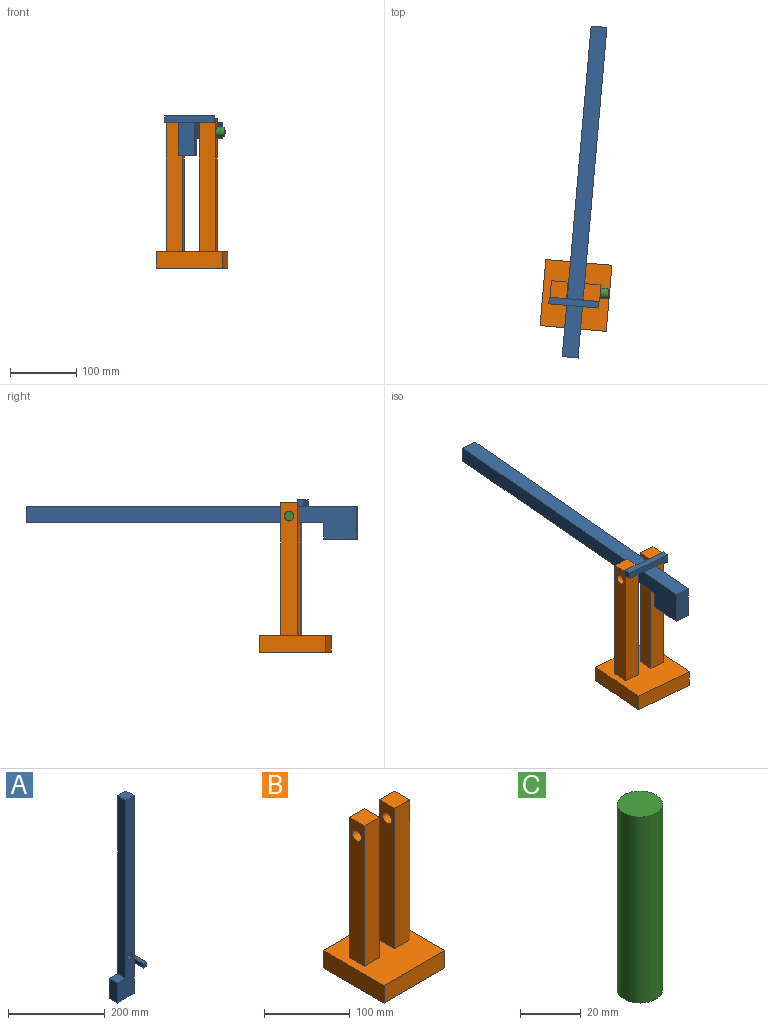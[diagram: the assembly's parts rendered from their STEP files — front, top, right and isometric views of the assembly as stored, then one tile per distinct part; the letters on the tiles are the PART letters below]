
ASSEMBLY  parts=3 mates=6
PART A: 17 faces, bbox 59x75x500 mm
  f0: plane 77.5x24mm, normal (1,0,0), area 1860mm2, adj f3,f4,f6,f11
  f1: plane 412.5x24mm, normal (1,0,0), area 9900mm2, adj f3,f4,f5,f13
  f2: plane 450x24mm, normal (-1,0,0), area 10800mm2, adj f3,f4,f5,f8
  f3: plane 500x49mm, normal (0,1,0), area 13073.3mm2, adj f0,f1,f2,f5,f6,f7,f8,f9
  f4: plane 500x49mm, normal (0,-1,0), area 13073.3mm2, adj f0,f1,f2,f5,f6,f7,f8,f9
  f5: plane 24x24mm, normal (0,0,1), area 576mm2, adj f1,f2,f3,f4
  f6: plane 49x24mm, normal (0,0,-1), area 1176mm2, adj f0,f3,f4,f9
  f7: cylinder r=7.5mm len=24mm, axis (0,-1,0), area 1131mm2, adj f3,f4
  f8: plane 25x24mm, normal (0,0,1), area 600mm2, adj f2,f3,f4,f9
  f9: plane 50x24mm, normal (-1,0,0), area 1200mm2, adj f3,f4,f6,f8
  f10: plane 27.1x10mm, normal (-1,0,0), area 271mm2, adj f4,f11,f13,f14
  f11: plane 75x10mm, normal (0,0,-1), area 750mm2, adj f0,f10,f12,f14,f15,f16
  f12: plane 10x10mm, normal (0,1,0), area 100mm2, adj f11,f13,f15,f16
  f13: plane 75x10mm, normal (0,0,1), area 750mm2, adj f1,f10,f12,f14,f15,f16
  f14: plane 10x10mm, normal (0,-1,0), area 100mm2, adj f10,f11,f13,f15
  f15: plane 75x10mm, normal (1,0,0), area 750mm2, adj f11,f12,f13,f14
  f16: plane 23.9x10mm, normal (-1,0,0), area 239mm2, adj f3,f11,f12,f13
PART B: 18 faces, bbox 100x100x225 mm
  f0: plane 100x100mm, normal (0,0,1), area 8750mm2, adj f1,f2,f3,f4,f6,f7,f8,f9
  f1: plane 100x25mm, normal (0,1,0), area 2500mm2, adj f0,f2,f4,f5
  f2: plane 100x25mm, normal (-1,0,0), area 2500mm2, adj f0,f1,f3,f5
  f3: plane 100x25mm, normal (0,-1,0), area 2500mm2, adj f0,f2,f4,f5
  f4: plane 100x25mm, normal (1,0,0), area 2500mm2, adj f0,f1,f3,f5
  f5: plane 100x100mm, normal (0,0,-1), area 10000mm2, adj f1,f2,f3,f4
  f6: plane 200x25mm, normal (1,0,0), area 4823.3mm2, adj f0,f7,f9,f10,f17
  f7: plane 200x25mm, normal (0,1,0), area 5000mm2, adj f0,f6,f8,f10
  f8: plane 200x25mm, normal (-1,0,0), area 4823.3mm2, adj f0,f7,f9,f10,f17
  f9: plane 200x25mm, normal (0,-1,0), area 5000mm2, adj f0,f6,f8,f10
  f10: plane 25x25mm, normal (0,0,1), area 625mm2, adj f6,f7,f8,f9
  f11: plane 200x25mm, normal (-1,0,0), area 4823.3mm2, adj f0,f12,f14,f15,f16
  f12: plane 200x25mm, normal (0,-1,0), area 5000mm2, adj f0,f11,f13,f15
  f13: plane 200x25mm, normal (1,0,0), area 4823.3mm2, adj f0,f12,f14,f15,f16
  f14: plane 200x25mm, normal (0,1,0), area 5000mm2, adj f0,f11,f13,f15
  f15: plane 25x25mm, normal (0,0,1), area 625mm2, adj f11,f12,f13,f14
  f16: cylinder r=7.5mm len=25mm, axis (1,0,0), area 1178.1mm2, adj f11,f13
  f17: cylinder r=7.5mm len=25mm, axis (1,0,0), area 1178.1mm2, adj f6,f8
PART C: 3 faces, bbox 14.9x14.9x75 mm
  f0: cylinder r=7.45mm len=75mm, axis (0,0,-1), area 3510.7mm2, adj f1,f2
  f1: plane 14.9x14.9mm, normal (0,0,1), area 174.4mm2, adj f0
  f2: plane 14.9x14.9mm, normal (0,0,-1), area 174.4mm2, adj f0
PLACE A rot(axis=(-0.59,-0.54,-0.59),122.9deg) t=(-150.28,-328.5,220.55)mm
PLACE B rot(axis=(0,0,-1),5deg) t=(-142.06,-228.83,13.2)mm
PLACE C rot(axis=(-0.71,0.03,0.71),176.5deg) t=(-92.25,-233.19,218.2)mm
MATE cylindrical C.f0 <-> B.f16  axis (-1,0.09,0) through (-166.97,-226.65,218.2)mm
MATE pin_slot A.f7 <-> C.f0  axis (1,-0.09,0) through (-129.61,-229.92,220.55)mm
MATE cylindrical B.f16 <-> C.f0  axis (1,-0.09,0) through (-104.7,-232.1,218.2)mm
MATE cylindrical C.f0 <-> B.f16  axis (-1,0.09,0) through (-166.97,-226.65,218.2)mm
MATE cylindrical C.f0 <-> B.f16  axis (1,-0.09,0) through (-92.25,-233.19,218.2)mm
MATE planar A.f3 <-> B.f16  axis (1,-0.09,0) through (-118.23,-99.91,218.2)mm
